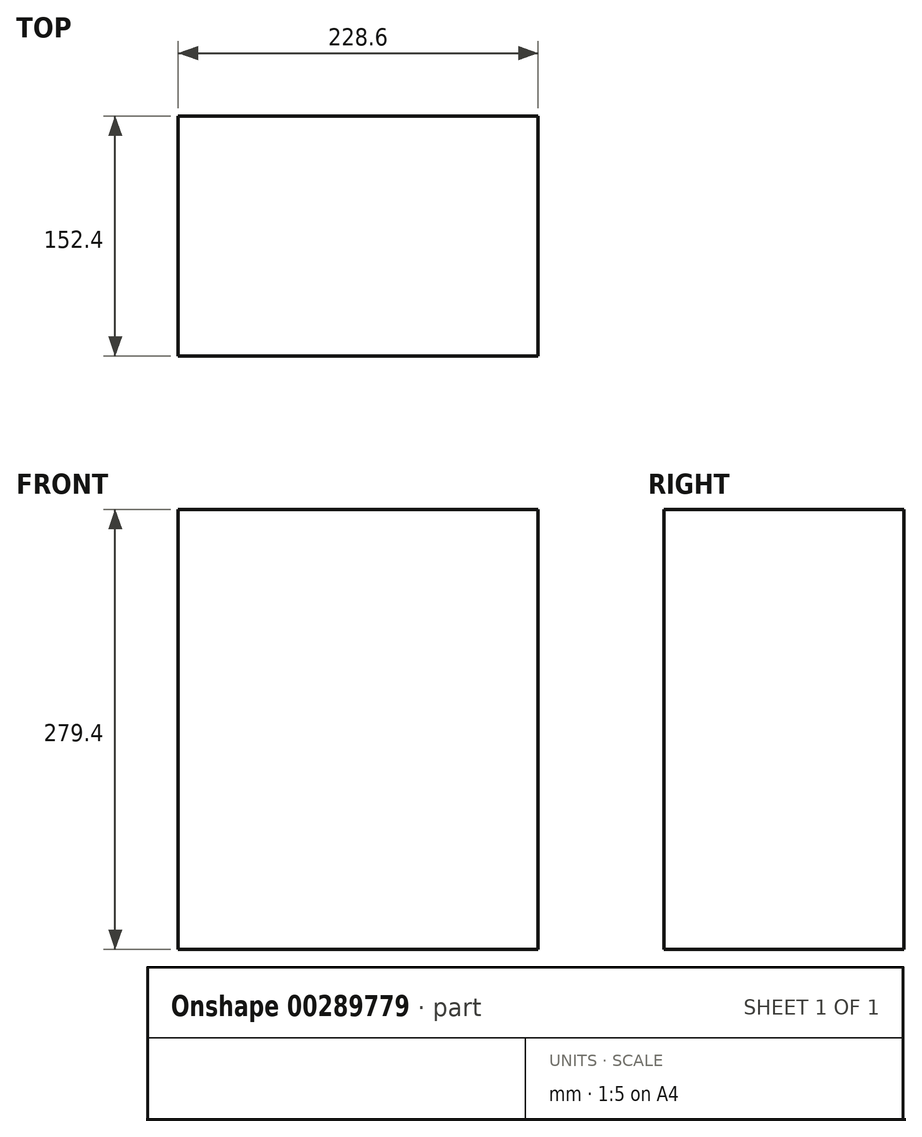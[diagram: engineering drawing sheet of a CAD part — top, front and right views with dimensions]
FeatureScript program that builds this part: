
annotation { "Feature Type Name" : "Feature", "Feature Type Description" : "" }
export const myFeature = defineFeature(function(context is Context, id is Id, definition is map)
    precondition{}
    {
        {
            var Q0;
            Q0=qCreatedBy(makeId("Top.planeOp"),FACE);
            var sketch = newSketch(context, id + "F0", { "sketchPlane" : qUnion([Q0])});
            skLineSegment(sketch, "E0.bottom", {"start": v(0, 0.01) * mm, "end": v(228.6, 0.01) * mm});
            skLineSegment(sketch, "E0.top", {"start": v(0, 152.41) * mm, "end": v(228.6, 152.41) * mm});
            skLineSegment(sketch, "E0.left", {"start": v(0, 0.01) * mm, "end": v(0, 152.41) * mm});
            skLineSegment(sketch, "E0.right", {"start": v(228.6, 0.01) * mm, "end": v(228.6, 152.41) * mm});
            skSolve(sketch);
        }
        {
            var Q0;
            Q0=makeQuery(id+"F0.imprint","IMPRINT",FACE,{"disambiguationData":[TD([[makeQuery(id+"F0.imprint","IMPRINT",EDGE,{"derivedFrom":sQuery(id+"F0.wireOp",EDGE,"E0.bottom")}),1.0]])]});
            extrude(context, id + "F1", {"entities" : qUnion([Q0]), "depth" : 279.4 * mm});
        }
    });
